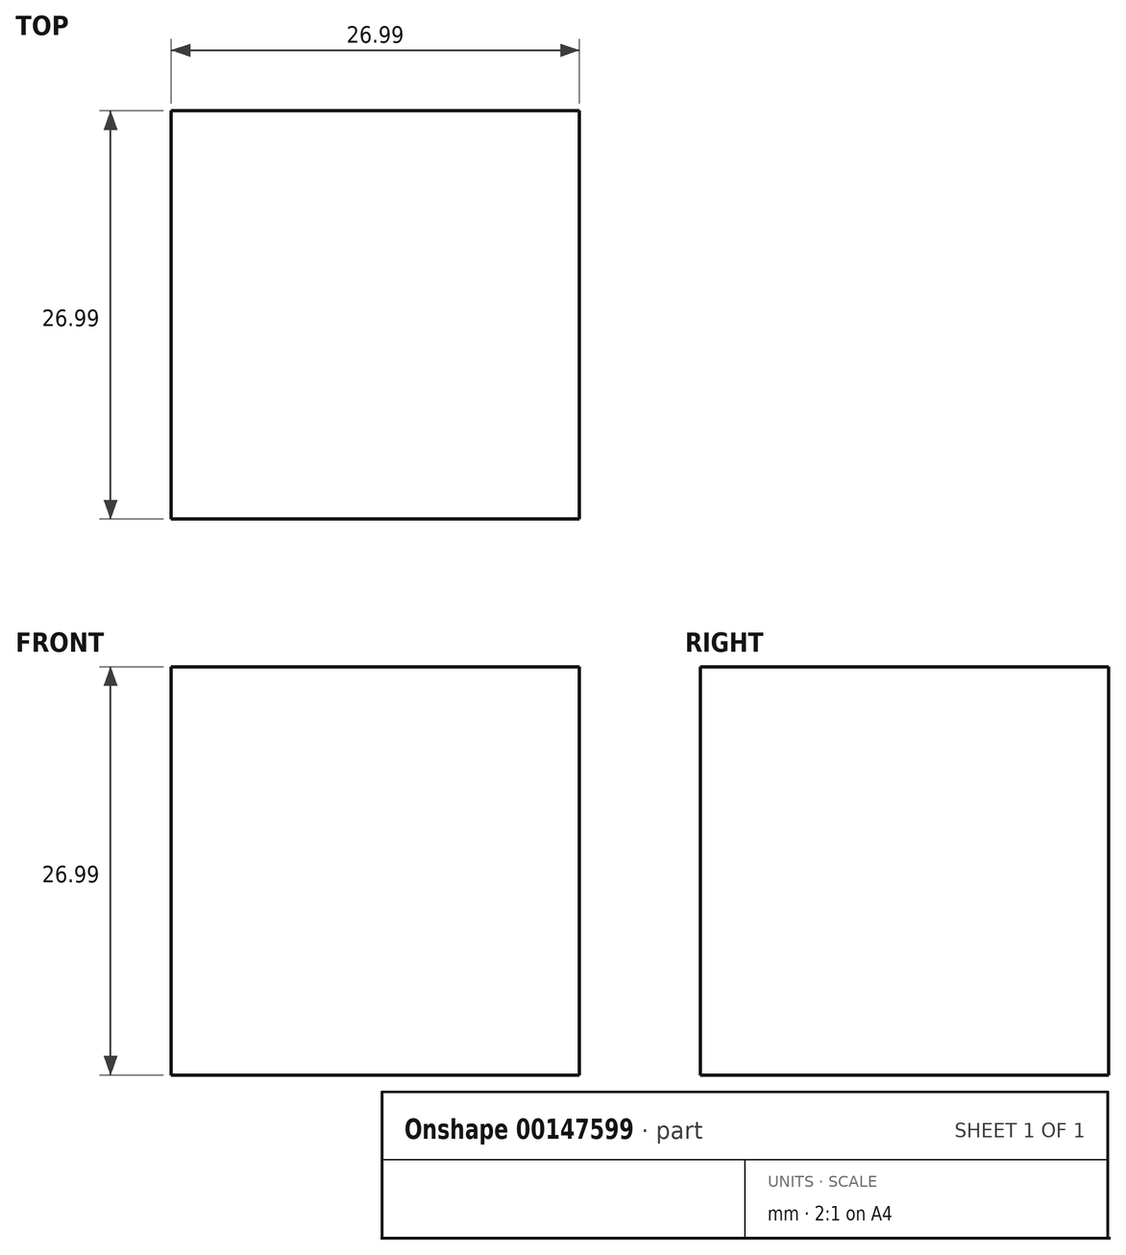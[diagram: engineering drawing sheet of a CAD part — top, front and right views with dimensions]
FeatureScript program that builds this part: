
annotation { "Feature Type Name" : "Feature", "Feature Type Description" : "" }
export const myFeature = defineFeature(function(context is Context, id is Id, definition is map)
    precondition{}
    {
        {
            var Q0;
            Q0=qCreatedBy(makeId("Top.planeOp"),FACE);
            var sketch = newSketch(context, id + "F0", { "sketchPlane" : qUnion([Q0])});
            skLineSegment(sketch, "E0.bottom", {"start": v(0, 0) * mm, "end": v(26.99, 0) * mm});
            skLineSegment(sketch, "E0.top", {"start": v(0, -26.99) * mm, "end": v(26.99, -26.99) * mm});
            skLineSegment(sketch, "E0.left", {"start": v(0, 0) * mm, "end": v(0, -26.99) * mm});
            skLineSegment(sketch, "E0.right", {"start": v(26.99, 0) * mm, "end": v(26.99, -26.99) * mm});
            skSolve(sketch);
        }
        {
            var Q0;
            Q0=qSketchRegion(id+"F0",true);
            extrude(context, id + "F1", {"entities" : qUnion([Q0]), "depth" : 26.99 * mm});
        }
    });
